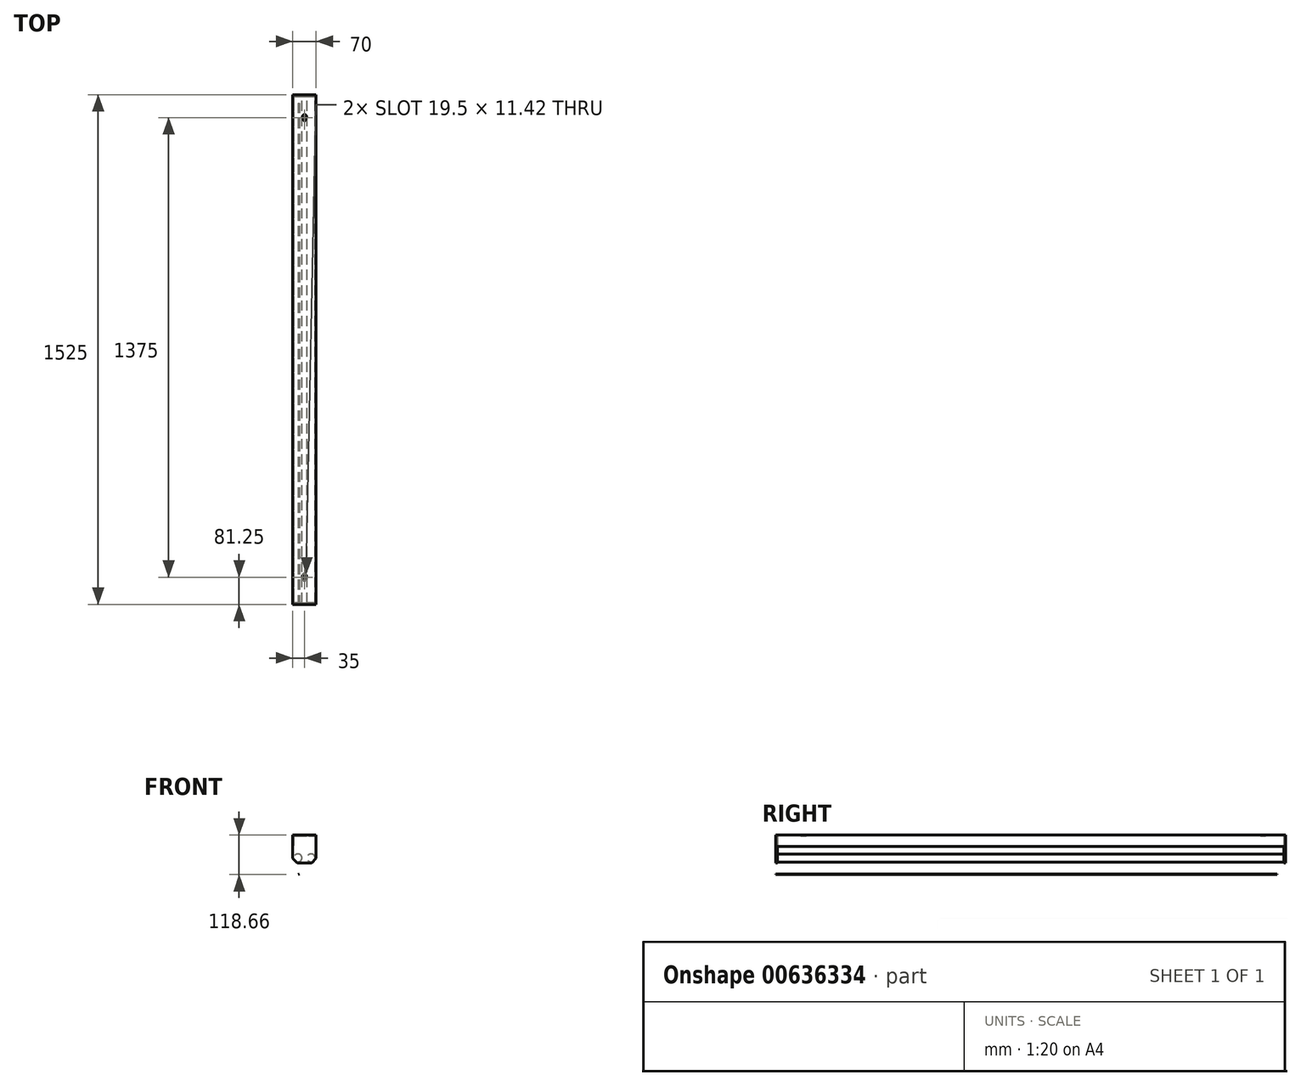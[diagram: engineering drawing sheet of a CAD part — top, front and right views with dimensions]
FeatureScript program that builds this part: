
annotation { "Feature Type Name" : "Feature", "Feature Type Description" : "" }
export const myFeature = defineFeature(function(context is Context, id is Id, definition is map)
    precondition{}
    {
        {
            var Q0;
            Q0=qCreatedBy(makeId("Front.planeOp"),FACE);
            var sketch = newSketch(context, id + "F0", { "sketchPlane" : qUnion([Q0])});
            skLineSegment(sketch, "E0", {"start": v(-35, 84) * mm, "end": v(35, 84) * mm});
            skLineSegment(sketch, "E1", {"start": v(35, 84) * mm, "end": v(35, 14) * mm});
            skLineSegment(sketch, "E2", {"start": v(22, 0) * mm, "end": v(35, 14) * mm});
            skLineSegment(sketch, "E3", {"start": v(22, 0) * mm, "end": v(-22, 0) * mm});
            skLineSegment(sketch, "E4", {"start": v(-22, 0) * mm, "end": v(-35, 14) * mm});
            skLineSegment(sketch, "E5", {"start": v(-35, 14) * mm, "end": v(-35, 84) * mm});
            skLineSegment(sketch, "E6", {"start": v(0, 44.81) * mm, "end": v(0, -20.6) * mm, "construction": true});
            skSolve(sketch);
        }
        {
            var Q0;
            Q0=makeQuery(id+"F0.imprint","IMPRINT",FACE,{"disambiguationData":[TD([[makeQuery(id+"F0.imprint","IMPRINT",EDGE,{"derivedFrom":sQuery(id+"F0.wireOp",EDGE,"E0")}),-1.0]])]});
            extrude(context, id + "F1", {"entities" : qUnion([Q0]), "oppositeDirection" : true, "depth" : 1525 * mm, "offsetDistance" : 25 * mm});
        }
        {
            var Q0;
            Q0=makeQuery(id+"F1.opExtrude","SWEPT_FACE",FACE,{"disambiguationData":[OSD([sQuery(id+"F0.wireOp",EDGE,"E1")])]});
            var sketch = newSketch(context, id + "F2", { "sketchPlane" : qUnion([Q0])});
            skLineSegment(sketch, "E7.bottom", {"start": v(5, 50) * mm, "end": v(1520, 50) * mm});
            skLineSegment(sketch, "E7.top", {"start": v(5, 0) * mm, "end": v(1520, 0) * mm});
            skLineSegment(sketch, "E7.left", {"start": v(5, 50) * mm, "end": v(5, 0) * mm});
            skLineSegment(sketch, "E7.right", {"start": v(1520, 50) * mm, "end": v(1520, 0) * mm});
            skSolve(sketch);
        }
        {
            var Q0;
            Q0 = qSketchRegion(id + "F2", true);
            extrude(context, id + "F3", {"entities" : qUnion([Q0]), "operationType" : NewBodyOperationType.REMOVE, "oppositeDirection" : true, "depth" : 80 * mm, "offsetDistance" : 25 * mm});
        }
        {
            var Q0;
            Q0=makeQuery(id+"F3.boolean.opBoolean","COPY",FACE,{"derivedFrom":makeQuery(id+"F3.opExtrude","SWEPT_FACE",FACE,{"disambiguationData":[OSD([sQuery(id+"F2.wireOp",EDGE,"E7.right")])]})});
            var sketch = newSketch(context, id + "F4", { "sketchPlane" : qUnion([Q0])});
            skCircle(sketch, "E8", {"center": v(-19.7, 15.17) * mm, "radius": 12 * mm});
            skCircle(sketch, "E9", {"center": v(19.7, 15.17) * mm, "radius": 12 * mm});
            skLineSegment(sketch, "E10", {"start": v(-28.5, 7) * mm, "end": v(0, 33.46) * mm, "construction": true});
            skPoint(sketch, "E10.startSnap0", {"position": v(-28.5, 7) * mm});
            skLineSegment(sketch, "E11", {"start": v(0, 33.46) * mm, "end": v(28.5, 7) * mm, "construction": true});
            skSolve(sketch);
        }
        {
            var Q0;
            Q0=makeQuery(id+"F4.imprint","IMPRINT",FACE,{"disambiguationData":[TD([[makeQuery(id+"F4.imprint","IMPRINT",EDGE,{"derivedFrom":sQuery(id+"F4.wireOp",EDGE,"E8")}),1.0]])]});
            var Q1;
            Q1=makeQuery(id+"F4.imprint","IMPRINT",FACE,{"disambiguationData":[TD([[makeQuery(id+"F4.imprint","IMPRINT",EDGE,{"derivedFrom":sQuery(id+"F4.wireOp",EDGE,"E9")}),1.0]])]});
            var Q2;
            Q2=makeQuery(id+"F3.boolean.opBoolean","COPY",FACE,{"derivedFrom":makeQuery(id+"F3.opExtrude","SWEPT_FACE",FACE,{"disambiguationData":[OSD([sQuery(id+"F2.wireOp",EDGE,"E7.left")])]})});
            extrude(context, id + "F5", {"entities" : qUnion([Q0, Q1]), "operationType" : NewBodyOperationType.ADD, "endBound" : BoundingType.UP_TO_SURFACE, "depth" : 25 * mm, "endBoundEntityFace" : qUnion([Q2]), "offsetDistance" : 25 * mm});
        }
        {
            var Q0;
            Q0=makeQuery(id+"F1.opExtrude","SWEPT_FACE",FACE,{"disambiguationData":[OSD([sQuery(id+"F0.wireOp",EDGE,"E0")])]});
            var sketch = newSketch(context, id + "F6", { "sketchPlane" : qUnion([Q0])});
            skArc(sketch, "E12", {"start": v(-3.5, 75) * mm, "mid": v(0, 71.5) * mm, "end": v(3.5, 75) * mm});
            skArc(sketch, "E13", {"start": v(3.5, 80.13) * mm, "mid": v(0, 91) * mm, "end": v(-3.5, 80.13) * mm});
            skLineSegment(sketch, "E14", {"start": v(-3.5, 75) * mm, "end": v(-3.5, 80.13) * mm});
            skLineSegment(sketch, "E15", {"start": v(3.5, 75) * mm, "end": v(3.5, 80.13) * mm});
            skArc(sketch, "E16", {"start": v(-3.5, 1450) * mm, "mid": v(0, 1446.5) * mm, "end": v(3.5, 1450) * mm});
            skArc(sketch, "E17", {"start": v(3.5, 1455.13) * mm, "mid": v(0, 1466) * mm, "end": v(-3.5, 1455.13) * mm});
            skLineSegment(sketch, "E18", {"start": v(-3.5, 1450) * mm, "end": v(-3.5, 1455.13) * mm});
            skLineSegment(sketch, "E19", {"start": v(3.5, 1450) * mm, "end": v(3.5, 1455.13) * mm});
            skSolve(sketch);
        }
        {
            var Q0;
            Q0=makeQuery(id+"F3.boolean.opBoolean","COPY",FACE,{"derivedFrom":makeQuery(id+"F3.opExtrude","SWEPT_FACE",FACE,{"disambiguationData":[OSD([sQuery(id+"F2.wireOp",EDGE,"E7.bottom")])]})});
            var sketch = newSketch(context, id + "F7", { "sketchPlane" : qUnion([Q0])});
            skLineSegment(sketch, "E20.bottom", {"start": v(-33, -1520) * mm, "end": v(33, -1520) * mm});
            skLineSegment(sketch, "E20.top", {"start": v(-33, -5) * mm, "end": v(33, -5) * mm});
            skLineSegment(sketch, "E20.left", {"start": v(-33, -1520) * mm, "end": v(-33, -5) * mm});
            skLineSegment(sketch, "E20.right", {"start": v(33, -1520) * mm, "end": v(33, -5) * mm});
            skSolve(sketch);
        }
        {
            var Q0;
            Q0 = qSketchRegion(id + "F7", true);
            extrude(context, id + "F8", {"entities" : qUnion([Q0]), "operationType" : NewBodyOperationType.REMOVE, "oppositeDirection" : true, "depth" : 32 * mm, "offsetDistance" : 25 * mm});
        }
        {
            var Q0;
            Q0 = qSketchRegion(id + "F6", true);
            var Q1;
            Q1=makeQuery(id+"F8.boolean.opBoolean","COPY",FACE,{"derivedFrom":makeQuery(id+"F8.opExtrude","CAP_FACE",FACE,{"disambiguationData":[OSD([sQuery(id+"F7.wireOp",EDGE,"E20.bottom"),sQuery(id+"F7.wireOp",EDGE,"E20.top"),sQuery(id+"F7.wireOp",EDGE,"E20.left"),sQuery(id+"F7.wireOp",EDGE,"E20.right")])],"isStart":false})});
            extrude(context, id + "F9", {"entities" : qUnion([Q0]), "operationType" : NewBodyOperationType.REMOVE, "endBound" : BoundingType.UP_TO_SURFACE, "oppositeDirection" : true, "depth" : 25 * mm, "endBoundEntityFace" : qUnion([Q1]), "offsetDistance" : 25 * mm});
        }
        {
            var Q0;
            Q0=qCreatedBy(makeId("Front.planeOp"),FACE);
            var sketch = newSketch(context, id + "F10", { "sketchPlane" : qUnion([Q0])});
            skLineSegment(sketch, "E21", {"start": v(-80, -35) * mm, "end": v(-80, 35) * mm, "construction": true});
            skFitSpline(sketch, "E22", {"points": [v(-140, -35) * mm, v(-80, 35) * mm, v(-20, -35) * mm], "startDerivative": vector(120, 360) * mm, "endDerivative": vector(120, -360) * mm});
            skLineSegment(sketch, "E23", {"start": v(-140, -35) * mm, "end": v(-144.7, -33.29) * mm});
            skLineSegment(sketch, "E24", {"start": v(-20, -35) * mm, "end": v(-15.3, -33.29) * mm});
            skLineSegment(sketch, "E25", {"start": v(-140, -35) * mm, "end": v(-20, -35) * mm, "construction": true});
            skFitSpline(sketch, "E26.0", {"points": [v(-140.95, -34.68) * mm, v(-135.94, -19.64) * mm, v(-128.4, -1.76) * mm, v(-118.32, 14.64) * mm, v(-110.72, 23.68) * mm, v(-103.06, 29.9) * mm, v(-95.35, 33.76) * mm, v(-88.93, 35.36) * mm, v(-83.82, 35.92) * mm, v(-80, 36.04) * mm, v(-76.18, 35.92) * mm, v(-71.07, 35.36) * mm, v(-64.65, 33.76) * mm, v(-56.94, 29.9) * mm, v(-49.28, 23.68) * mm, v(-41.68, 14.64) * mm, v(-31.6, -1.76) * mm, v(-24.06, -19.64) * mm, v(-19.05, -34.68) * mm]});
            skLineSegment(sketch, "E27.0", {"start": v(-139.66, -34.06) * mm, "end": v(-139.68, -34.05) * mm});
            skLineSegment(sketch, "E28.0", {"start": v(-20.34, -34.06) * mm, "end": v(-20.32, -34.05) * mm});
            skLineSegment(sketch, "E29", {"start": v(-15.64, -32.35) * mm, "end": v(-15.3, -33.29) * mm});
            skLineSegment(sketch, "E30", {"start": v(-144.36, -32.35) * mm, "end": v(-144.7, -33.29) * mm});
            skFitSpline(sketch, "E31.trimOffspring", {"points": [v(-140.95, -34.68) * mm, v(-135.94, -19.64) * mm, v(-128.4, -1.76) * mm, v(-118.32, 14.64) * mm, v(-110.72, 23.68) * mm, v(-103.06, 29.9) * mm, v(-95.35, 33.76) * mm, v(-88.93, 35.36) * mm, v(-83.82, 35.92) * mm, v(-80, 36.04) * mm, v(-76.18, 35.92) * mm, v(-71.07, 35.36) * mm, v(-64.65, 33.76) * mm, v(-56.94, 29.9) * mm, v(-49.28, 23.68) * mm, v(-41.68, 14.64) * mm, v(-31.6, -1.76) * mm, v(-24.06, -19.64) * mm, v(-19.05, -34.68) * mm]});
            skLineSegment(sketch, "E32.trimOffspring", {"start": v(-140.62, -33.7) * mm, "end": v(-144.36, -32.35) * mm});
            skFitSpline(sketch, "E33.trimOffspring", {"points": [v(-140.95, -34.68) * mm, v(-135.94, -19.64) * mm, v(-128.4, -1.76) * mm, v(-118.32, 14.64) * mm, v(-110.72, 23.68) * mm, v(-103.06, 29.9) * mm, v(-95.35, 33.76) * mm, v(-88.93, 35.36) * mm, v(-83.82, 35.92) * mm, v(-80, 36.04) * mm, v(-76.18, 35.92) * mm, v(-71.07, 35.36) * mm, v(-64.65, 33.76) * mm, v(-56.94, 29.9) * mm, v(-49.28, 23.68) * mm, v(-41.68, 14.64) * mm, v(-31.6, -1.76) * mm, v(-24.06, -19.64) * mm, v(-19.05, -34.68) * mm]});
            skLineSegment(sketch, "E34.trimOffspring", {"start": v(-19.38, -33.7) * mm, "end": v(-15.64, -32.35) * mm});
            skSolve(sketch);
        }
        {
            var Q0;
            {var subQ1=sQuery(id+"F10.wireOp",EDGE,"E29");Q0=makeQuery(id+"F10.imprint","IMPRINT",FACE,{"disambiguationData":[TD([[makeQuery(id+"F10.imprint","IMPRINT",EDGE,{"derivedFrom":subQ1}),-1.0]])]});}
            extrude(context, id + "F11", {"entities" : qUnion([Q0]), "oppositeDirection" : true, "depth" : 1500 * mm, "offsetDistance" : 25 * mm});
        }
    });
